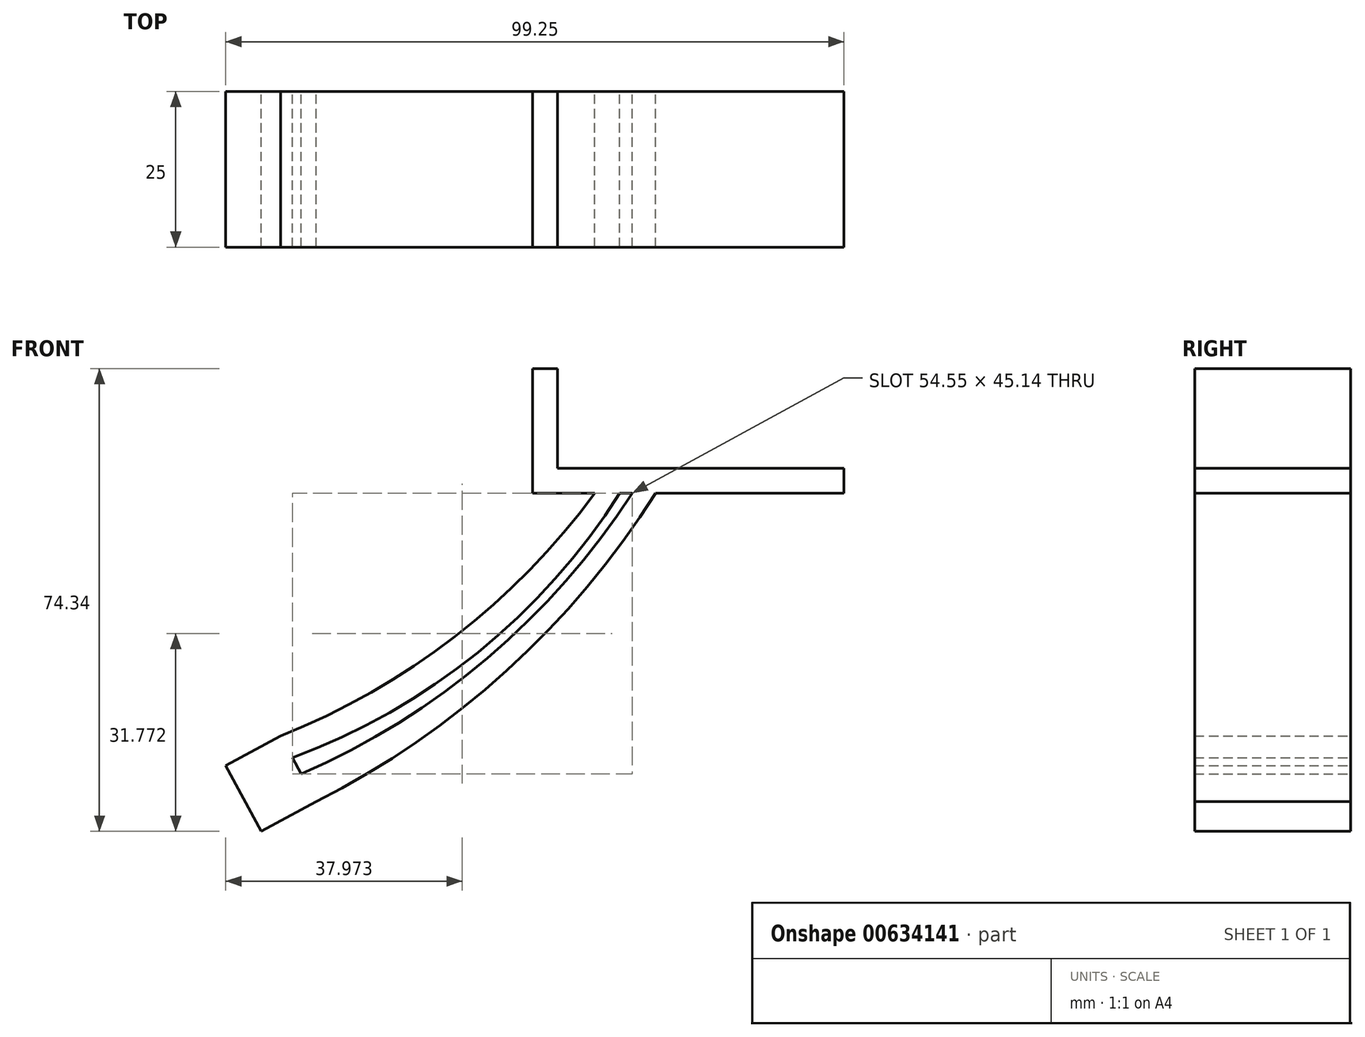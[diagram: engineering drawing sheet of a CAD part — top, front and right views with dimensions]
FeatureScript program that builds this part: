
annotation { "Feature Type Name" : "Feature", "Feature Type Description" : "" }
export const myFeature = defineFeature(function(context is Context, id is Id, definition is map)
    precondition{}
    {
        {
            var Q0;
            Q0=qCreatedBy(makeId("Front.planeOp"),FACE);
            var sketch = newSketch(context, id + "F0", { "sketchPlane" : qUnion([Q0])});
            skLineSegment(sketch, "E0.bottom", {"start": v(0, 0) * mm, "end": v(4, 0) * mm});
            skLineSegment(sketch, "E0.top", {"start": v(0, 20) * mm, "end": v(4, 20) * mm});
            skLineSegment(sketch, "E0.left", {"start": v(0, 0) * mm, "end": v(0, 20) * mm});
            skLineSegment(sketch, "E0.right", {"start": v(4, 0) * mm, "end": v(4, 20) * mm});
            skLineSegment(sketch, "E1", {"start": v(0, 0) * mm, "end": v(50, 0) * mm});
            skLineSegment(sketch, "E2", {"start": v(50, 4) * mm, "end": v(0, 4) * mm});
            skLineSegment(sketch, "E3", {"start": v(50, 0) * mm, "end": v(50, 4) * mm});
            skLineSegment(sketch, "E4", {"start": v(0, 0) * mm, "end": v(10, 0) * mm});
            skLineSegment(sketch, "E5", {"start": v(10, 0) * mm, "end": v(14, 0) * mm});
            skLineSegment(sketch, "E6", {"start": v(-40.46, -39.02) * mm, "end": v(-34.74, -49.57) * mm});
            skLineSegment(sketch, "E7", {"start": v(-40.46, -39.02) * mm, "end": v(-38.55, -42.54) * mm});
            skArc(sketch, "E8", {"start": v(-38.55, -42.54) * mm, "mid": v(-8.78, -25.6) * mm, "end": v(14, 0) * mm});
            skArc(sketch, "E9", {"start": v(-40.46, -39.02) * mm, "mid": v(-12.48, -23.07) * mm, "end": v(10, 0) * mm});
            skLineSegment(sketch, "E10", {"start": v(14, 0) * mm, "end": v(16, 0) * mm});
            skLineSegment(sketch, "E11", {"start": v(16, 0) * mm, "end": v(19.76, 0) * mm});
            skLineSegment(sketch, "E12", {"start": v(16, 0) * mm, "end": v(18.98, 0) * mm});
            skArc(sketch, "E13", {"start": v(-37.14, -45.14) * mm, "mid": v(-7.22, -26.51) * mm, "end": v(16, 0) * mm});
            skArc(sketch, "E14", {"start": v(-34.74, -49.57) * mm, "mid": v(-4.11, -28.5) * mm, "end": v(19.76, 0) * mm});
            skLineSegment(sketch, "E15", {"start": v(-40.46, -39.02) * mm, "end": v(-49.25, -43.79) * mm});
            skLineSegment(sketch, "E16", {"start": v(-49.25, -43.79) * mm, "end": v(-43.53, -54.34) * mm});
            skLineSegment(sketch, "E17", {"start": v(-43.53, -54.34) * mm, "end": v(-34.74, -49.57) * mm});
            skSolve(sketch);
        }
        {
            var Q0;
            Q0 = qSketchRegion(id + "F0", true);
            extrude(context, id + "F1", {"entities" : qUnion([Q0]), "depth" : 25 * mm, "offsetDistance" : 25 * mm});
        }
    });
